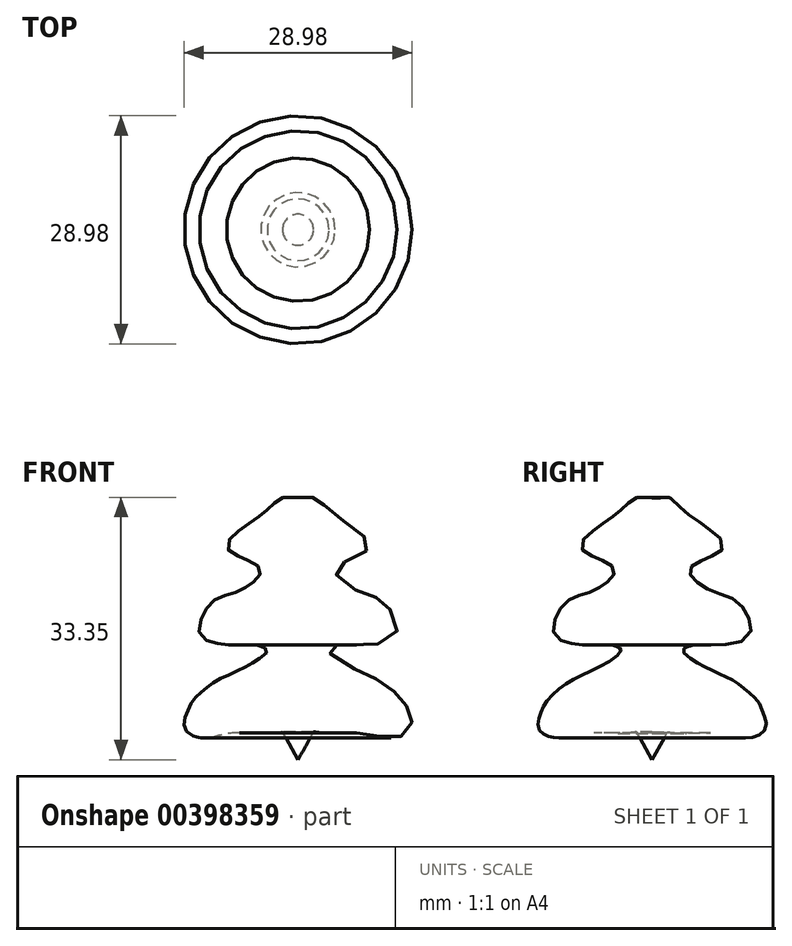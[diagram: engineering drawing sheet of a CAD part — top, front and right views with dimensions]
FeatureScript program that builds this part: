
annotation { "Feature Type Name" : "Feature", "Feature Type Description" : "" }
export const myFeature = defineFeature(function(context is Context, id is Id, definition is map)
    precondition{}
    {
        {
            var Q0;
            Q0=qCreatedBy(makeId("Front.planeOp"),FACE);
            var sketch = newSketch(context, id + "F0", { "sketchPlane" : qUnion([Q0])});
            skLineSegment(sketch, "E0", {"start": v(0, 0) * mm, "end": v(0, 33.3) * mm});
            skFitSpline(sketch, "E1", {"points": [v(0, 33.3) * mm, v(1.58, 33.3) * mm, v(2.17, 33.3) * mm, v(3.94, 31.73) * mm, v(7.69, 28.97) * mm, v(9.07, 27) * mm, v(6.1, 25.22) * mm, v(4.73, 23.85) * mm, v(7.49, 21.48) * mm, v(10.25, 20.5) * mm, v(12.02, 18.52) * mm, v(12.22, 15.57) * mm, v(6.9, 14.58) * mm, v(5.32, 14.58) * mm, v(4.53, 14.39) * mm, v(3.94, 13.8) * mm, v(8.28, 11.04) * mm, v(10.64, 9.85) * mm, v(13.4, 7.49) * mm, v(14, 6.3) * mm, v(14.39, 3.94) * mm, v(11.82, 2.76) * mm, v(8.87, 3.35) * mm, v(3.94, 3.35) * mm, v(1.97, 3.55) * mm, v(1.58, 3.55) * mm], "startDerivative": vector(55.67, -2.2) * mm, "endDerivative": vector(-20.88, -1.33) * mm});
            skFitSpline(sketch, "E2", {"points": [v(1.97, 3.55) * mm, v(0, 0) * mm], "startDerivative": vector(-1.97, -3.55) * mm, "endDerivative": vector(-1.97, -3.55) * mm});
            skSolve(sketch);
        }
        {
            var Q0;
            {var subQ0=sQuery(id+"F0.wireOp",EDGE,"E0");Q0=makeQuery(id+"F0.imprint","IMPRINT",FACE,{"disambiguationData":[TD([[makeQuery(id+"F0.imprint","IMPRINT",EDGE,{"derivedFrom":subQ0}),-1.0]])]});}
            var Q1;
            Q1=sQuery(id+"F0.wireOp",EDGE,"E0");
            revolve(context, id + "F1", {"entities" : qUnion([Q0]), "axis" : qUnion([Q1]), "revolveType" : RevolveType.FULL});
        }
    });
